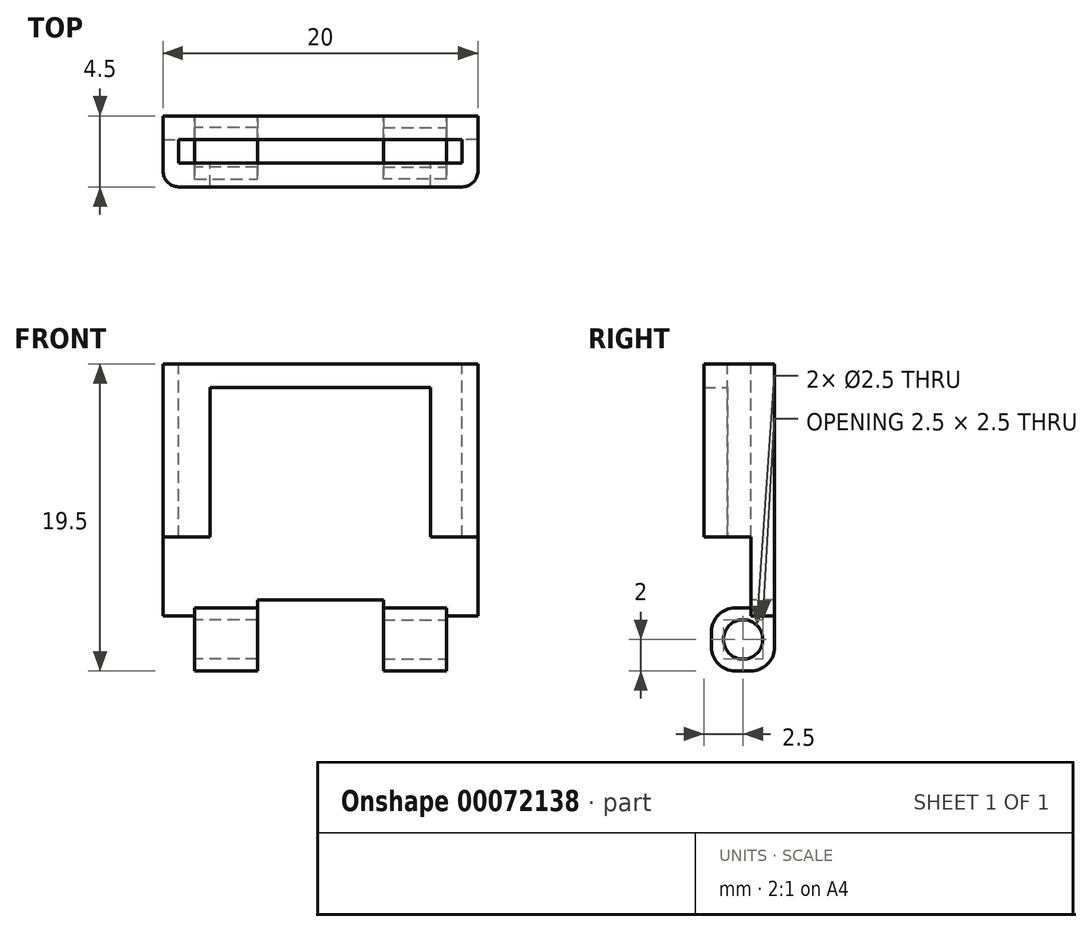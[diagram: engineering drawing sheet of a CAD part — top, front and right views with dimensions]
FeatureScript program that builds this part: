
annotation { "Feature Type Name" : "Feature", "Feature Type Description" : "" }
export const myFeature = defineFeature(function(context is Context, id is Id, definition is map)
    precondition{}
    {
        {
            var Q0;
            Q0=qCreatedBy(makeId("Front.planeOp"),FACE);
            var sketch = newSketch(context, id + "F0", { "sketchPlane" : qUnion([Q0])});
            skLineSegment(sketch, "E0.bottom", {"start": v(0, 0) * mm, "end": v(-10, 0) * mm});
            skLineSegment(sketch, "E0.top", {"start": v(0, 16) * mm, "end": v(-10, 16) * mm});
            skLineSegment(sketch, "E0.left", {"start": v(0, 0) * mm, "end": v(0, 16) * mm});
            skLineSegment(sketch, "E0.right", {"start": v(-10, 0) * mm, "end": v(-10, 16) * mm});
            skSolve(sketch);
        }
        {
            var Q0;
            Q0 = qSketchRegion(id + "F0", true);
            extrude(context, id + "F1", {"entities" : qUnion([Q0]), "depth" : 1.5 * mm});
        }
        {
            var Q0;
            Q0=makeQuery(id+"F1.opExtrude","CAP_FACE",FACE,{"disambiguationData":[OSD([sQuery(id+"F0.wireOp",EDGE,"E0.bottom"),sQuery(id+"F0.wireOp",EDGE,"E0.top"),sQuery(id+"F0.wireOp",EDGE,"E0.left"),sQuery(id+"F0.wireOp",EDGE,"E0.right")])],"isStart":false});
            var sketch = newSketch(context, id + "F2", { "sketchPlane" : qUnion([Q0])});
            skLineSegment(sketch, "E1.bottom", {"start": v(-8, 0.5) * mm, "end": v(-4, 0.5) * mm});
            skLineSegment(sketch, "E1.top", {"start": v(-8, -3.5) * mm, "end": v(-4, -3.5) * mm});
            skLineSegment(sketch, "E1.left", {"start": v(-8, 0.5) * mm, "end": v(-8, -3.5) * mm});
            skLineSegment(sketch, "E1.right", {"start": v(-4, 0.5) * mm, "end": v(-4, -3.5) * mm});
            skSolve(sketch);
        }
        {
            var Q0;
            Q0 = qSketchRegion(id + "F2", true);
            extrude(context, id + "F3", {"entities" : qUnion([Q0]), "operationType" : NewBodyOperationType.ADD, "depth" : 2.5 * mm, "hasSecondDirection" : true, "secondDirectionOppositeDirection" : true, "secondDirectionDepth" : 1.5 * mm});
        }
        {
            var Q0;
            Q0=makeQuery(id+"F3.opExtrude","CAP_EDGE",EDGE,{"disambiguationData":[OSD([sQuery(id+"F2.wireOp",EDGE,"E1.top")])],"isStart":true});
            var Q1;
            Q1=makeQuery(id+"F3.opExtrude","CAP_EDGE",EDGE,{"disambiguationData":[OSD([sQuery(id+"F2.wireOp",EDGE,"E1.top")])],"isStart":false});
            var Q2;
            Q2=makeQuery(id+"F3.opExtrude","CAP_EDGE",EDGE,{"disambiguationData":[OSD([sQuery(id+"F2.wireOp",EDGE,"E1.bottom")])],"isStart":false});
            fillet(context, id + "F4", {"entities" : qUnion([Q0, Q1, Q2]), "radius" : 1.5 * mm, "tangentPropagation" : true, "allowEdgeOverflow" : false});
        }
        {
            var Q0;
            Q0=makeQuery(id+"F3.opExtrude","SWEPT_FACE",FACE,{"disambiguationData":[OSD([sQuery(id+"F2.wireOp",EDGE,"E1.left")])]});
            var sketch = newSketch(context, id + "F5", { "sketchPlane" : qUnion([Q0])});
            skCircle(sketch, "E2", {"center": v(2, -1.5) * mm, "radius": 1.25 * mm});
            skPoint(sketch, "E2.centerSnap0", {"position": v(4, -1.5) * mm});
            skSolve(sketch);
        }
        {
            var Q0;
            Q0 = qSketchRegion(id + "F5", true);
            extrude(context, id + "F6", {"entities" : qUnion([Q0]), "operationType" : NewBodyOperationType.REMOVE, "endBound" : BoundingType.THROUGH_ALL, "oppositeDirection" : true, "depth" : 25 * mm});
        }
        {
            var Q0;
            Q0=makeQuery(id+"F1.opExtrude","CAP_FACE",FACE,{"disambiguationData":[OSD([sQuery(id+"F0.wireOp",EDGE,"E0.bottom"),sQuery(id+"F0.wireOp",EDGE,"E0.top"),sQuery(id+"F0.wireOp",EDGE,"E0.left"),sQuery(id+"F0.wireOp",EDGE,"E0.right")])],"isStart":false});
            var sketch = newSketch(context, id + "F7", { "sketchPlane" : qUnion([Q0])});
            skLineSegment(sketch, "E3.top", {"start": v(-10, 5) * mm, "end": v(-7, 5) * mm});
            skLineSegment(sketch, "E3.left", {"start": v(-10, 16) * mm, "end": v(-10, 5) * mm});
            skLineSegment(sketch, "E3.right", {"start": v(-7, 14.5) * mm, "end": v(-7, 5) * mm});
            skLineSegment(sketch, "E4.bottom", {"start": v(-10, 16) * mm, "end": v(0, 16) * mm});
            skLineSegment(sketch, "E4.top", {"start": v(-7, 14.5) * mm, "end": v(0, 14.5) * mm});
            skLineSegment(sketch, "E5", {"start": v(0, 16) * mm, "end": v(0, 14.5) * mm});
            skSolve(sketch);
        }
        {
            var Q0;
            Q0 = qSketchRegion(id + "F7", true);
            extrude(context, id + "F8", {"entities" : qUnion([Q0]), "operationType" : NewBodyOperationType.ADD, "depth" : 3 * mm});
        }
        {
            var Q0;
            Q0=makeQuery(id+"F8.boolean.opBoolean","MERGE",FACE,{"derivedFrom":[makeQuery(id+"F1.opExtrude","SWEPT_FACE",FACE,{"disambiguationData":[OSD([sQuery(id+"F0.wireOp",EDGE,"E0.top")])]}),makeQuery(id+"F8.opExtrude","SWEPT_FACE",FACE,{"disambiguationData":[OSD([sQuery(id+"F7.wireOp",EDGE,"E3.bottom")])]})]});
            var sketch = newSketch(context, id + "F9", { "sketchPlane" : qUnion([Q0])});
            skLineSegment(sketch, "E6.bottom", {"start": v(0, -1.5) * mm, "end": v(-9, -1.5) * mm});
            skLineSegment(sketch, "E6.top", {"start": v(0, -3) * mm, "end": v(-9, -3) * mm});
            skLineSegment(sketch, "E6.left", {"start": v(0, -1.5) * mm, "end": v(0, -3) * mm});
            skLineSegment(sketch, "E6.right", {"start": v(-9, -1.5) * mm, "end": v(-9, -3) * mm});
            skSolve(sketch);
        }
        {
            var Q0;
            Q0=makeQuery(id+"F8.opExtrude","CAP_EDGE",EDGE,{"disambiguationData":[OSD([sQuery(id+"F7.wireOp",EDGE,"E3.left")])],"isStart":false});
            fillet(context, id + "F10", {"entities" : qUnion([Q0]), "radius" : 1 * mm, "tangentPropagation" : true, "allowEdgeOverflow" : false});
        }
        {
            var Q0;
            Q0 = qSketchRegion(id + "F9", true);
            extrude(context, id + "F11", {"entities" : qUnion([Q0]), "operationType" : NewBodyOperationType.REMOVE, "endBound" : BoundingType.UP_TO_NEXT, "oppositeDirection" : true, "depth" : 25 * mm});
        }
        {
            var Q0;
            Q0=makeQuery(id+"F11.boolean.opBoolean","MERGE",FACE,{"derivedFrom":[makeQuery(id+"F1.opExtrude","CAP_FACE",FACE,{"disambiguationData":[OSD([sQuery(id+"F0.wireOp",EDGE,"E0.bottom"),sQuery(id+"F0.wireOp",EDGE,"E0.top"),sQuery(id+"F0.wireOp",EDGE,"E0.left"),sQuery(id+"F0.wireOp",EDGE,"E0.right")])],"isStart":false}),makeQuery(id+"F11.opExtrude","SWEPT_FACE",FACE,{"disambiguationData":[OSD([sQuery(id+"F9.wireOp",EDGE,"E6.bottom")])]})]});
            var sketch = newSketch(context, id + "F12", { "sketchPlane" : qUnion([Q0])});
            skLineSegment(sketch, "E7.bottom", {"start": v(-4, 0) * mm, "end": v(0, 0) * mm});
            skLineSegment(sketch, "E7.top", {"start": v(-4, 1) * mm, "end": v(0, 1) * mm});
            skLineSegment(sketch, "E7.left", {"start": v(-4, 0) * mm, "end": v(-4, 1) * mm});
            skLineSegment(sketch, "E7.right", {"start": v(0, 0) * mm, "end": v(0, 1) * mm});
            skSolve(sketch);
        }
        {
            var Q0;
            Q0 = qSketchRegion(id + "F12", true);
            extrude(context, id + "F13", {"entities" : qUnion([Q0]), "operationType" : NewBodyOperationType.REMOVE, "oppositeDirection" : true, "depth" : 1.5 * mm});
        }
        {
            var Q0;
            Q0=makeQuery(id+"F1.opExtrude","SWEPT_BODY",BODY,{"disambiguationData":[OSD([sQuery(id+"F0.wireOp",EDGE,"E0.bottom"),sQuery(id+"F0.wireOp",EDGE,"E0.top"),sQuery(id+"F0.wireOp",EDGE,"E0.left"),sQuery(id+"F0.wireOp",EDGE,"E0.right")])]});
            var Q1;
            Q1=qCreatedBy(makeId("Right.planeOp"),FACE);
            mirror(context, id + "F14", {"operationType" : NewBodyOperationType.ADD, "entities" : qUnion([Q0]), "mirrorPlane" : qUnion([Q1])});
        }
    });
